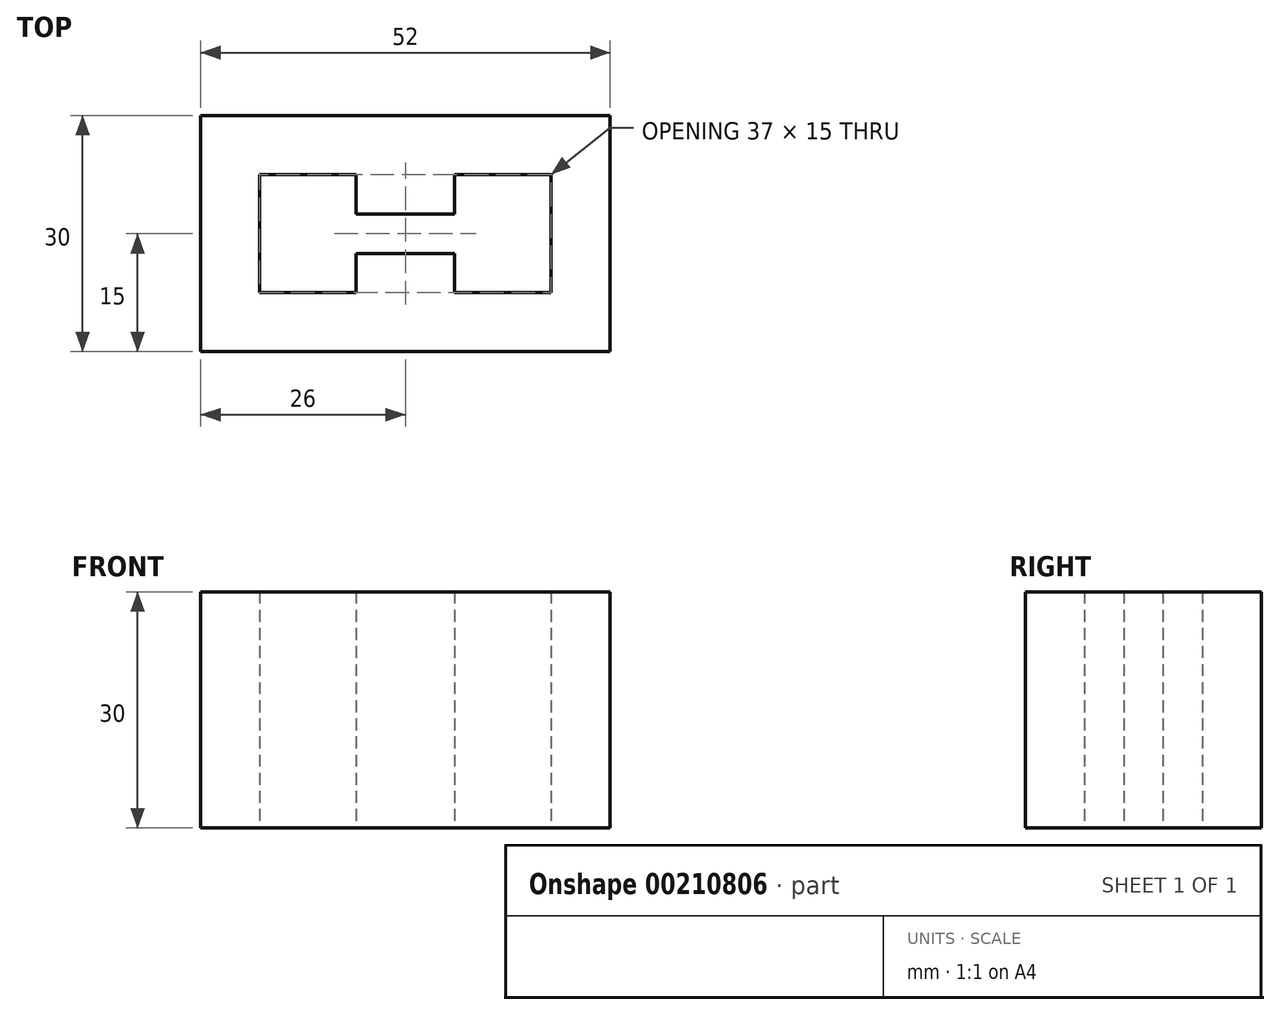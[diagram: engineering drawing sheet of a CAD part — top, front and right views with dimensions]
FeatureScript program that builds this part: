
annotation { "Feature Type Name" : "Feature", "Feature Type Description" : "" }
export const myFeature = defineFeature(function(context is Context, id is Id, definition is map)
    precondition{}
    {
        {
            var Q0;
            Q0=qCreatedBy(makeId("Top.planeOp"),FACE);
            var sketch = newSketch(context, id + "F0", { "sketchPlane" : qUnion([Q0])});
            skLineSegment(sketch, "E0.bottom", {"start": v(0, 0) * mm, "end": v(52, 0) * mm});
            skLineSegment(sketch, "E0.top", {"start": v(0, 30) * mm, "end": v(52, 30) * mm});
            skLineSegment(sketch, "E0.left", {"start": v(0, 0) * mm, "end": v(0, 30) * mm});
            skLineSegment(sketch, "E0.right", {"start": v(52, 0) * mm, "end": v(52, 30) * mm});
            skLineSegment(sketch, "E1", {"start": v(7.5, 22.5) * mm, "end": v(7.5, 7.5) * mm});
            skLineSegment(sketch, "E2", {"start": v(7.5, 7.5) * mm, "end": v(19.75, 7.5) * mm});
            skLineSegment(sketch, "E3", {"start": v(19.75, 7.5) * mm, "end": v(19.75, 12.5) * mm});
            skLineSegment(sketch, "E4", {"start": v(19.75, 12.5) * mm, "end": v(32.25, 12.5) * mm});
            skLineSegment(sketch, "E5", {"start": v(32.25, 12.5) * mm, "end": v(32.25, 7.5) * mm});
            skLineSegment(sketch, "E6", {"start": v(32.25, 7.5) * mm, "end": v(44.5, 7.5) * mm});
            skLineSegment(sketch, "E7", {"start": v(7.5, 22.5) * mm, "end": v(19.75, 22.5) * mm});
            skLineSegment(sketch, "E8", {"start": v(19.75, 22.5) * mm, "end": v(19.75, 17.5) * mm});
            skLineSegment(sketch, "E9", {"start": v(19.75, 17.5) * mm, "end": v(32.25, 17.5) * mm});
            skLineSegment(sketch, "E10", {"start": v(32.25, 17.5) * mm, "end": v(32.25, 22.5) * mm});
            skLineSegment(sketch, "E11", {"start": v(32.25, 22.5) * mm, "end": v(44.5, 22.5) * mm});
            skLineSegment(sketch, "E12", {"start": v(44.5, 22.5) * mm, "end": v(44.5, 7.5) * mm});
            skSolve(sketch);
        }
        {
            var Q0;
            Q0=makeQuery(id+"F0.imprint","IMPRINT",FACE,{"disambiguationData":[TD([[makeQuery(id+"F0.imprint","IMPRINT",EDGE,{"derivedFrom":sQuery(id+"F0.wireOp",EDGE,"E0.bottom")}),1.0]])]});
            extrude(context, id + "F1", {"entities" : qUnion([Q0]), "depth" : 30 * mm});
        }
    });
